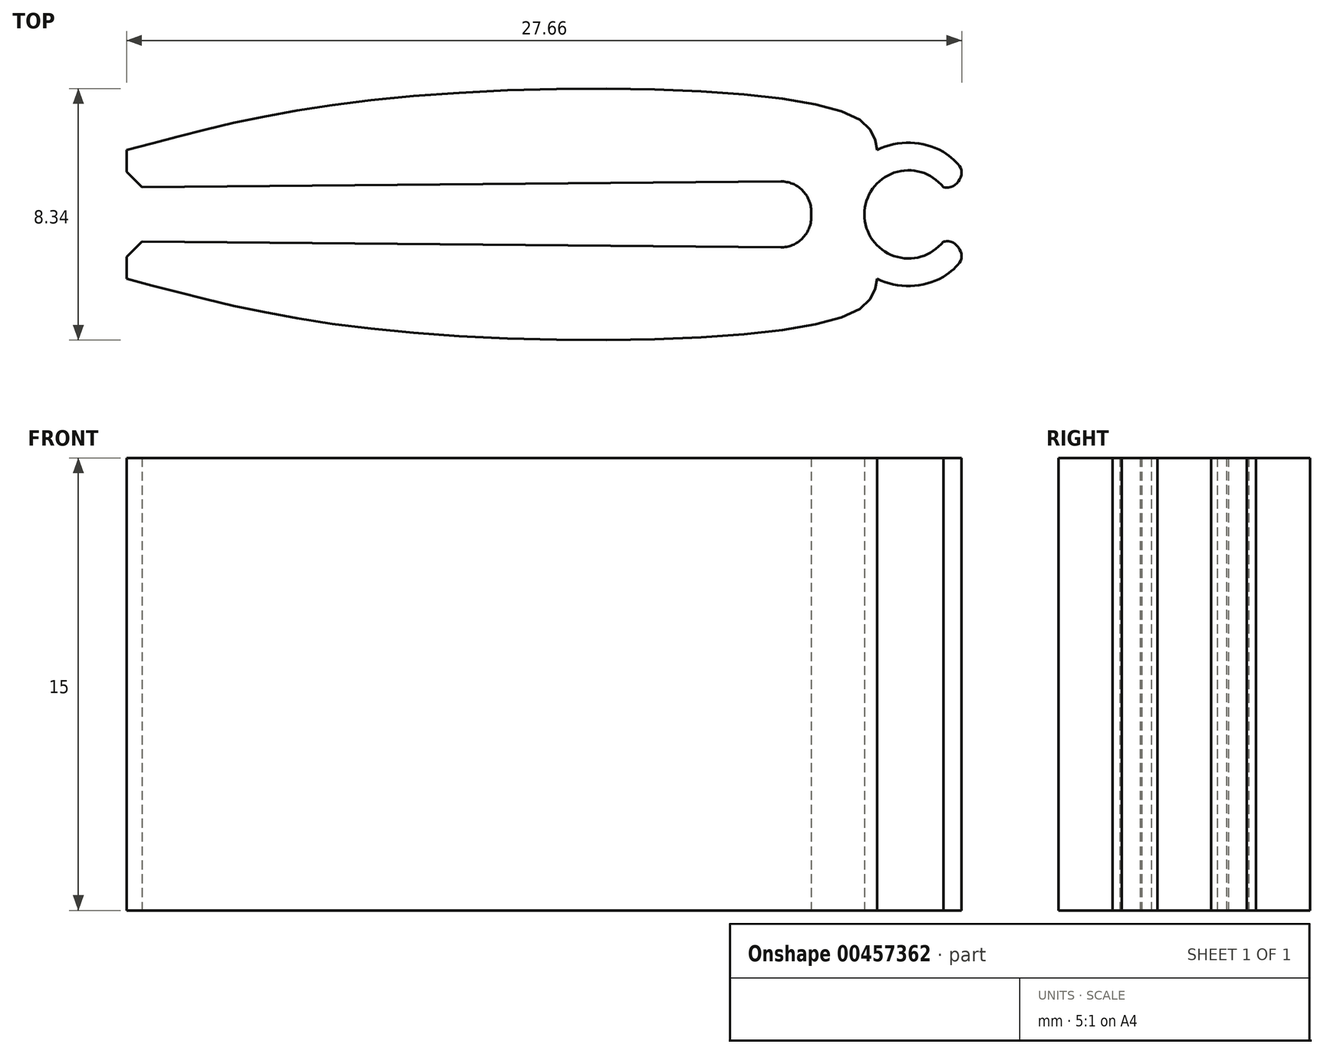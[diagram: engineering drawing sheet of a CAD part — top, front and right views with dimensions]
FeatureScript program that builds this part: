
annotation { "Feature Type Name" : "Feature", "Feature Type Description" : "" }
export const myFeature = defineFeature(function(context is Context, id is Id, definition is map)
    precondition{}
    {
        {
            var Q0;
            Q0=qCreatedBy(makeId("Top.planeOp"),FACE);
            var sketch = newSketch(context, id + "F0", { "sketchPlane" : qUnion([Q0])});
            skPoint(sketch, "E0", {"position": v(16.79, 0.9) * mm});
            skPoint(sketch, "E1", {"position": v(16.79, -0.9) * mm});
            skArc(sketch, "E2", {"start": v(16.79, 0.9) * mm, "mid": v(14.18, 0) * mm, "end": v(16.79, -0.9) * mm});
            skPoint(sketch, "E3", {"position": v(16.79, 2.08) * mm});
            skPoint(sketch, "E4.MirrorP", {"position": v(16.79, -2.08) * mm});
            skArc(sketch, "E5", {"start": v(16.79, 2.08) * mm, "mid": v(13.26, 0) * mm, "end": v(16.79, -2.08) * mm});
            skFitSpline(sketch, "E6", {"points": [v(16.79, 2.08) * mm, v(17.4, 1.41) * mm, v(17.11, 0.94) * mm, v(16.79, 0.9) * mm], "startDerivative": vector(2.1, -1.5) * mm, "endDerivative": vector(-1.26, 0.16) * mm});
            skFitSpline(sketch, "E7.MirrorCS", {"points": [v(16.79, -2.08) * mm, v(17.4, -1.41) * mm, v(17.11, -0.94) * mm, v(16.79, -0.9) * mm], "startDerivative": vector(2.1, 1.5) * mm, "endDerivative": vector(-1.26, -0.16) * mm});
            skSolve(sketch);
        }
        {
            var Q0;
            Q0=makeQuery(id+"F0.imprint","IMPRINT",FACE,{"disambiguationData":[TD([[makeQuery(id+"F0.imprint","IMPRINT",EDGE,{"derivedFrom":sQuery(id+"F0.wireOp",EDGE,"E2")}),-1.0]])]});
            extrude(context, id + "F1", {"entities" : qUnion([Q0]), "endBound" : BoundingType.SYMMETRIC, "depth" : 15 * mm, "offsetDistance" : 25 * mm});
        }
        {
            var Q0;
            Q0=qCreatedBy(makeId("Top.planeOp"),FACE);
            var sketch = newSketch(context, id + "F2", { "sketchPlane" : qUnion([Q0])});
            skLineSegment(sketch, "E8.right", {"start": v(12.41, 0.1) * mm, "end": v(12.41, -0.1) * mm});
            skLineSegment(sketch, "E9", {"start": v(-10.26, 0.9) * mm, "end": v(11.4, 1.1) * mm});
            skLineSegment(sketch, "E10", {"start": v(-10.26, -0.9) * mm, "end": v(11.4, -1.1) * mm});
            skLineSegment(sketch, "E11", {"start": v(-10.26, 4.36) * mm, "end": v(-10.26, -3.88) * mm, "construction": true});
            skLineSegment(sketch, "E12", {"start": v(-10.26, 2.13) * mm, "end": v(-10.26, 0.9) * mm});
            skLineSegment(sketch, "E13", {"start": v(-10.26, -0.9) * mm, "end": v(-10.26, -2.13) * mm});
            skFitSpline(sketch, "E14", {"points": [v(-10.26, 2.13) * mm, v(-1.26, 3.88) * mm, v(13.93, 3.2) * mm, v(14.6, 2.13) * mm], "startDerivative": vector(19.35, 5.07) * mm, "endDerivative": vector(1.14, -7.45) * mm});
            skLineSegment(sketch, "E15", {"start": v(14.6, 2.13) * mm, "end": v(13.93, 1.53) * mm});
            skFitSpline(sketch, "E16.MirrorCS", {"points": [v(-10.26, -2.13) * mm, v(-1.26, -3.88) * mm, v(13.93, -3.2) * mm, v(14.6, -2.13) * mm], "startDerivative": vector(19.35, -5.07) * mm, "endDerivative": vector(1.14, 7.45) * mm});
            skLineSegment(sketch, "E17.MirrorCS", {"start": v(14.6, -2.13) * mm, "end": v(13.93, -1.53) * mm});
            skLineSegment(sketch, "E18", {"start": v(13.93, 1.53) * mm, "end": v(13.93, -1.53) * mm});
            skPoint(sketch, "E19.visualSharp", {"position": v(12.41, 1.1) * mm});
            skArc(sketch, "E19.filletArc", {"start": v(12.41, 0.1) * mm, "mid": v(12.12, 0.8) * mm, "end": v(11.4, 1.1) * mm});
            skPoint(sketch, "E20.visualSharp", {"position": v(12.41, -1.1) * mm});
            skArc(sketch, "E20.filletArc", {"start": v(11.4, -1.1) * mm, "mid": v(12.12, -0.8) * mm, "end": v(12.41, -0.1) * mm});
            skSolve(sketch);
        }
        {
            var Q0;
            Q0 = qSketchRegion(id + "F2", true);
            extrude(context, id + "F3", {"entities" : qUnion([Q0]), "operationType" : NewBodyOperationType.ADD, "endBound" : BoundingType.SYMMETRIC, "depth" : 15 * mm, "offsetDistance" : 25 * mm});
        }
        {
            var Q0;
            Q0=makeQuery(id+"F3.opExtrude","SWEPT_EDGE",EDGE,{"disambiguationData":[OSD([sQuery(id+"F2.wireOp",EDGE,"E10"),sQuery(id+"F2.wireOp",EDGE,"E13")])]});
            var Q1;
            Q1=makeQuery(id+"F3.opExtrude","SWEPT_EDGE",EDGE,{"disambiguationData":[OSD([sQuery(id+"F2.wireOp",EDGE,"E9"),sQuery(id+"F2.wireOp",EDGE,"E12")])]});
            chamfer(context, id + "F4", {"entities" : qUnion([Q0, Q1]), "width" : 0.5 * mm, "tangentPropagation" : true});
        }
    });
